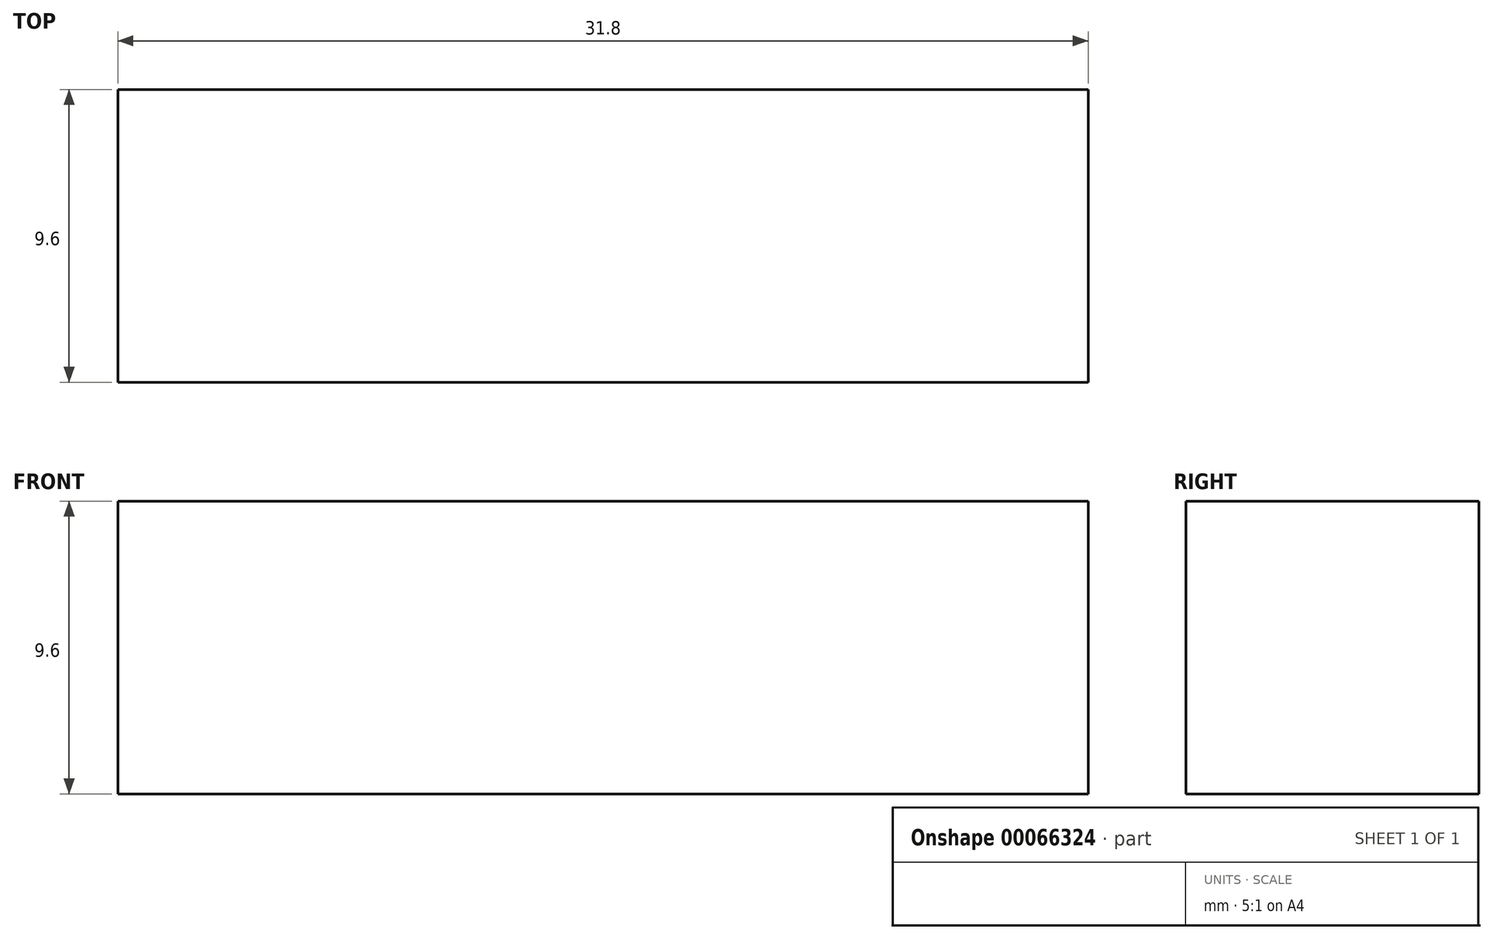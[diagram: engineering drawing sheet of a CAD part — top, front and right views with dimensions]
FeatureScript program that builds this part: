
annotation { "Feature Type Name" : "Feature", "Feature Type Description" : "" }
export const myFeature = defineFeature(function(context is Context, id is Id, definition is map)
    precondition{}
    {
        {
            var Q0;
            Q0=qCreatedBy(makeId("Top.planeOp"),FACE);
            var sketch = newSketch(context, id + "F0", { "sketchPlane" : qUnion([Q0])});
            skLineSegment(sketch, "E0.rect.bottom", {"start": v(15.9, 4.8) * mm, "end": v(-15.9, 4.8) * mm});
            skLineSegment(sketch, "E0.rect.top", {"start": v(15.9, -4.8) * mm, "end": v(-15.9, -4.8) * mm});
            skLineSegment(sketch, "E0.rect.left", {"start": v(15.9, 4.8) * mm, "end": v(15.9, -4.8) * mm});
            skLineSegment(sketch, "E0.rect.right", {"start": v(-15.9, 4.8) * mm, "end": v(-15.9, -4.8) * mm});
            skPoint(sketch, "E0.rect.middle", {"position": v(0, 0) * mm});
            skSolve(sketch);
        }
        {
            var Q0;
            Q0 = qSketchRegion(id + "F0", true);
            extrude(context, id + "F1", {"entities" : qUnion([Q0]), "depth" : 9.6 * mm});
        }
    });
